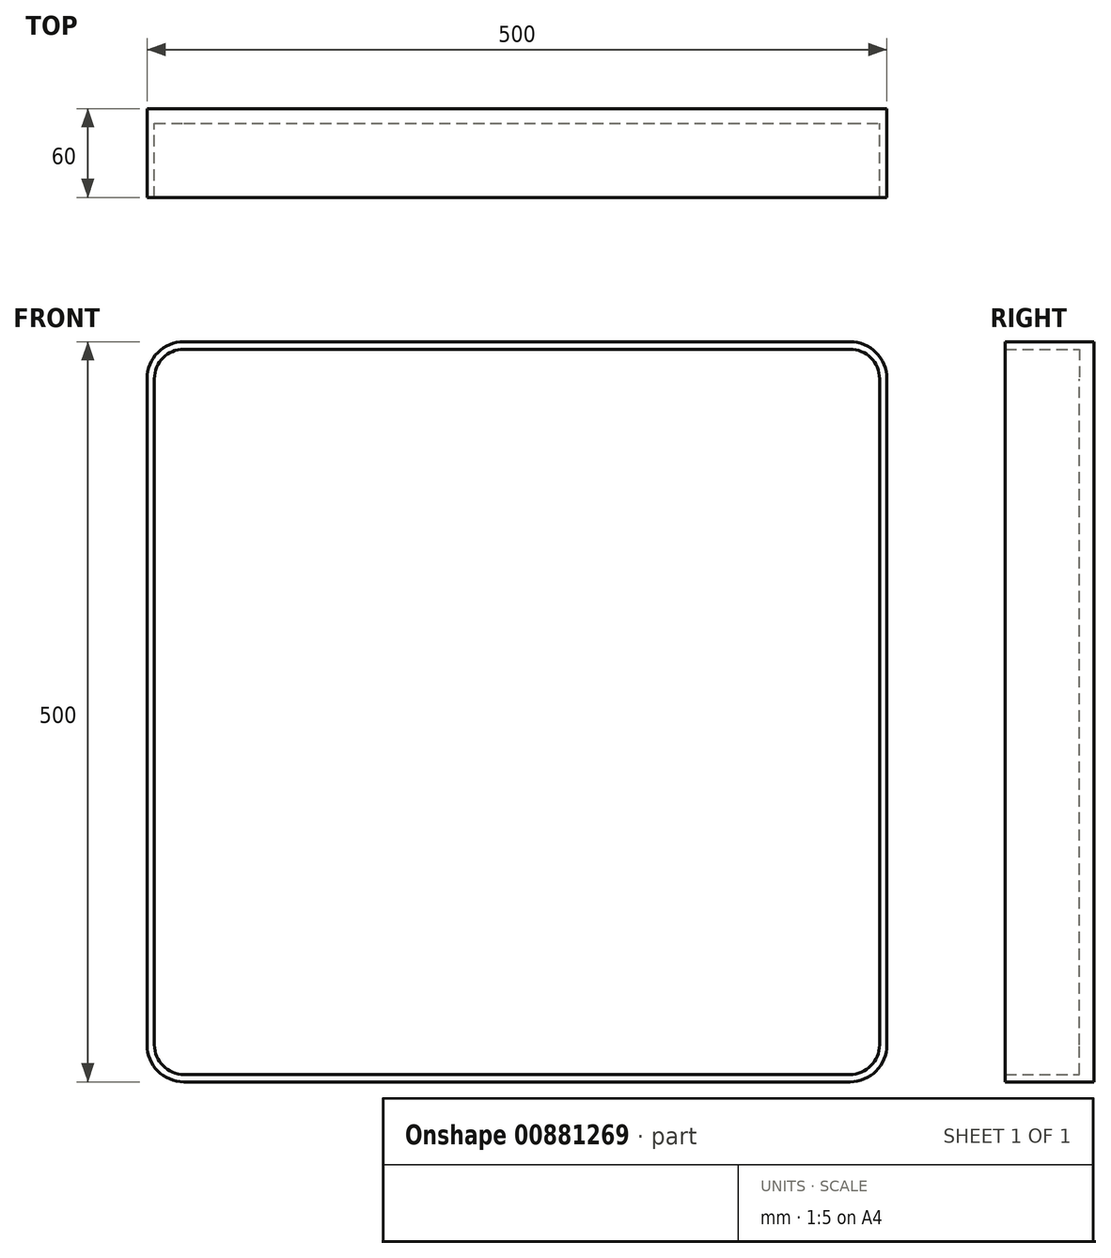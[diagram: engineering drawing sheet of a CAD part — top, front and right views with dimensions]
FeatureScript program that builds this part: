
annotation { "Feature Type Name" : "Feature", "Feature Type Description" : "" }
export const myFeature = defineFeature(function(context is Context, id is Id, definition is map)
    precondition{}
    {
        {
            var Q0;
            Q0=qCreatedBy(makeId("Front.planeOp"),FACE);
            var sketch = newSketch(context, id + "F0", { "sketchPlane" : qUnion([Q0])});
            skLineSegment(sketch, "E0", {"start": v(250, 20) * mm, "end": v(250, 245) * mm});
            skLineSegment(sketch, "E1", {"start": v(225, 270) * mm, "end": v(-225, 270) * mm});
            skLineSegment(sketch, "E2", {"start": v(-250, 245) * mm, "end": v(-250, -205) * mm});
            skLineSegment(sketch, "E3", {"start": v(-225, -230) * mm, "end": v(225, -230) * mm});
            skLineSegment(sketch, "E4", {"start": v(250, -205) * mm, "end": v(250, 20) * mm});
            skPoint(sketch, "E5.visualSharp", {"position": v(-250, 270) * mm});
            skArc(sketch, "E5.filletArc", {"start": v(-225, 270) * mm, "mid": v(-242.68, 262.68) * mm, "end": v(-250, 245) * mm});
            skPoint(sketch, "E6.visualSharp", {"position": v(-250, -230) * mm});
            skArc(sketch, "E6.filletArc", {"start": v(-250, -205) * mm, "mid": v(-242.68, -222.68) * mm, "end": v(-225, -230) * mm});
            skPoint(sketch, "E7.visualSharp", {"position": v(250, -230) * mm});
            skArc(sketch, "E7.filletArc", {"start": v(225, -230) * mm, "mid": v(242.68, -222.68) * mm, "end": v(250, -205) * mm});
            skPoint(sketch, "E8.visualSharp", {"position": v(250, 270) * mm});
            skArc(sketch, "E8.filletArc", {"start": v(250, 245) * mm, "mid": v(242.68, 262.68) * mm, "end": v(225, 270) * mm});
            skLineSegment(sketch, "E9.0", {"start": v(245, -205) * mm, "end": v(245, 20) * mm});
            skArc(sketch, "E9.1", {"start": v(225, -225) * mm, "mid": v(239.14, -219.14) * mm, "end": v(245, -205) * mm});
            skLineSegment(sketch, "E9.2", {"start": v(245, 20) * mm, "end": v(245, 245) * mm});
            skLineSegment(sketch, "E9.3", {"start": v(-225, -225) * mm, "end": v(225, -225) * mm});
            skArc(sketch, "E9.4", {"start": v(-245, -205) * mm, "mid": v(-239.14, -219.14) * mm, "end": v(-225, -225) * mm});
            skArc(sketch, "E9.5", {"start": v(245, 245) * mm, "mid": v(239.14, 259.14) * mm, "end": v(225, 265) * mm});
            skLineSegment(sketch, "E9.6", {"start": v(225, 265) * mm, "end": v(-225, 265) * mm});
            skArc(sketch, "E9.7", {"start": v(-225, 265) * mm, "mid": v(-239.14, 259.14) * mm, "end": v(-245, 245) * mm});
            skLineSegment(sketch, "E9.8", {"start": v(-245, 245) * mm, "end": v(-245, -205) * mm});
            skSolve(sketch);
        }
        {
            var Q0;
            Q0=makeQuery(id+"F0.imprint","IMPRINT",FACE,{"disambiguationData":[TD([[makeQuery(id+"F0.imprint","IMPRINT",EDGE,{"derivedFrom":sQuery(id+"F0.wireOp",EDGE,"E0")}),1.0]])]});
            extrude(context, id + "F1", {"entities" : qUnion([Q0]), "depth" : 60 * mm, "offsetDistance" : 25 * mm});
        }
        {
            var Q0;
            Q0=makeQuery(id+"F0.imprint","IMPRINT",FACE,{"disambiguationData":[TD([[makeQuery(id+"F0.imprint","IMPRINT",EDGE,{"derivedFrom":sQuery(id+"F0.wireOp",EDGE,"E9.0")}),1.0]])]});
            extrude(context, id + "F2", {"entities" : qUnion([Q0]), "operationType" : NewBodyOperationType.ADD, "depth" : 10 * mm, "offsetDistance" : 25 * mm});
        }
    });
